# Revit family: for update_56251XXX_new
name_source: partatom
category: Plumbing Fixtures
revit_build: Autodesk Revit 2018 (Build: 20170223_1515(x64)
units: mm (PartAtom-declared; Revit-internal decimal feet)

## family parameters
Cut with Voids When Loaded = Yes
Host = Face
OmniClass Number = 23.31.17.29
OmniClass Title = Shower Drains
Part Type = Normal
Room Calculation Point = No
Round Connector Dimension = Use Diameter
Shared = No

## types (2) — shared parameters
BIMobject category = Drainage
Connector Description = Water Outlet 40 mm
Description = RainDrain Brilliance Complete set point drain 150/150 tileable rear cover
Design country = Germany
Diameter = 40
Edition number = 1
IFC Classification = Pipe Fitting
Manufacturer = Hansgrohe
Manufacturer country = Germany
Manufacturer name = hansgrohe
Masterformat 2014 Code = 22 13 19.13
Masterformat 2014 Description = Sanitary Drains
Material 1 = Hansgrohe - Plastic - Black
Material 3 = Hansgrohe - Metal - Stainless Steel
Model = 56251XXX
OmniClass Code = 23-31 17 29
OmniClass Description = Shower Drains
Product Guid = c5d0e7f9-a944-498a-9dcb-b6c8fdb87137
Product SKU = 56251XXX
Product data url = https://bimobject.com
Product family = uBox universal
Product group = Concealed basic set shower drains
Product name = 56251XXX RainDrain Brilliance Complete set point drain 150/150 tileable rear cover
Product url = https://www.hansgrohe.com
QR code = https://bimobject.com
UNSPSC Code = 40141719
URL = https://www.hansgrohe.com
Uniclass 2015 Code = Pr_65_52_25
Uniclass 2015 Name = Drainage traps and accessories
Uniformat II Code = D2010
Uniformat II Description = Plumbing Fixtures
Weight Net (Kg) = 1.2
zero-valued in all types: Default Elevation

## per-type parameters (varying)
| type | Material 2 |
| 800 Stainless Steel Optic | Hansgrohe - Metal - 800 Stainless Steel Optic |
| 670 Matt Black | Hansgrohe - Metal - 670 Matt Black |

## geometry (parser evidence)
native form markers: Sweep x7
no freeform markers — native parametric forms only
